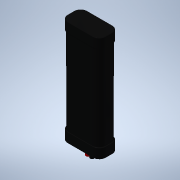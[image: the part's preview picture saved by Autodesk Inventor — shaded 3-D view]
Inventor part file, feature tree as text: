
AUTODESK INVENTOR PART (.ipt)
format: ipt  version: 2020 (Build 240168000, 168)  size: 385,024 bytes
history: native  units: mm
features: fillet x7, extrude x6, sketch x6, other x1
ambient origin geometry x8: Origin, YZ Plane, XZ Plane, XY Plane, X Axis, Y Axis, Z Axis, Center Point
bodies: Body1 (feature_tree)
feature tree (20):
  other  "Sólido1"
  extrude  "Extrusión1"  Depth=105.0mm
  extrude  "Extrusión2"  Depth=47.0mm
  extrude  "Extrusión3"  Depth=24.0mm
  extrude  "Extrusión4"  Depth=8.0mm TaperAngle=0.0deg
  fillet  "Empalme1"  Radius=12.0mm
  fillet  "Empalme2"  Radius=36.0mm
  fillet  "Empalme3"  Radius=5.5mm
  fillet  "Empalme4"  Radius=5.5mm
  fillet  "Empalme5"  Radius=3.0mm
  fillet  "Empalme6"  Radius=8.0mm
  fillet  "Empalme7"  Radius=8.0mm
  extrude  "Extrusión5"  Depth=4.0mm
  extrude  "Extrusión6"  Depth=0.5mm
  sketch  "Boceto1"  dims[d0=45.0mm d1=105.0mm]
  sketch  "Boceto2"  dims[d2=23.0mm d3=0.0mm d4=47.0mm]
  sketch  "Boceto3"  dims[d5=1.0mm d6=24.0mm]
  sketch  "Boceto4"  dims[d8=0.5mm d9=12.0mm d10=0.0mm d11=12.0mm d12=0.0mm d13=36.0mm d14=5.5mm d15=5.5mm d16=3.0mm d17=0.0mm d18=8.0mm d19=8.0mm]
  sketch  "Boceto5"  dims[d20=8.0mm d21=4.0mm]
  sketch  "Boceto6"  dims[d22=0.5mm d23=0.5mm d24=0.5mm d26=5.0mm d29=6.0mm d30=15.0mm d31=9.0mm d32=0.0mm d33=5.0mm d34=5.0mm d35=0.0mm d36=9.0mm d37=0.0mm]
